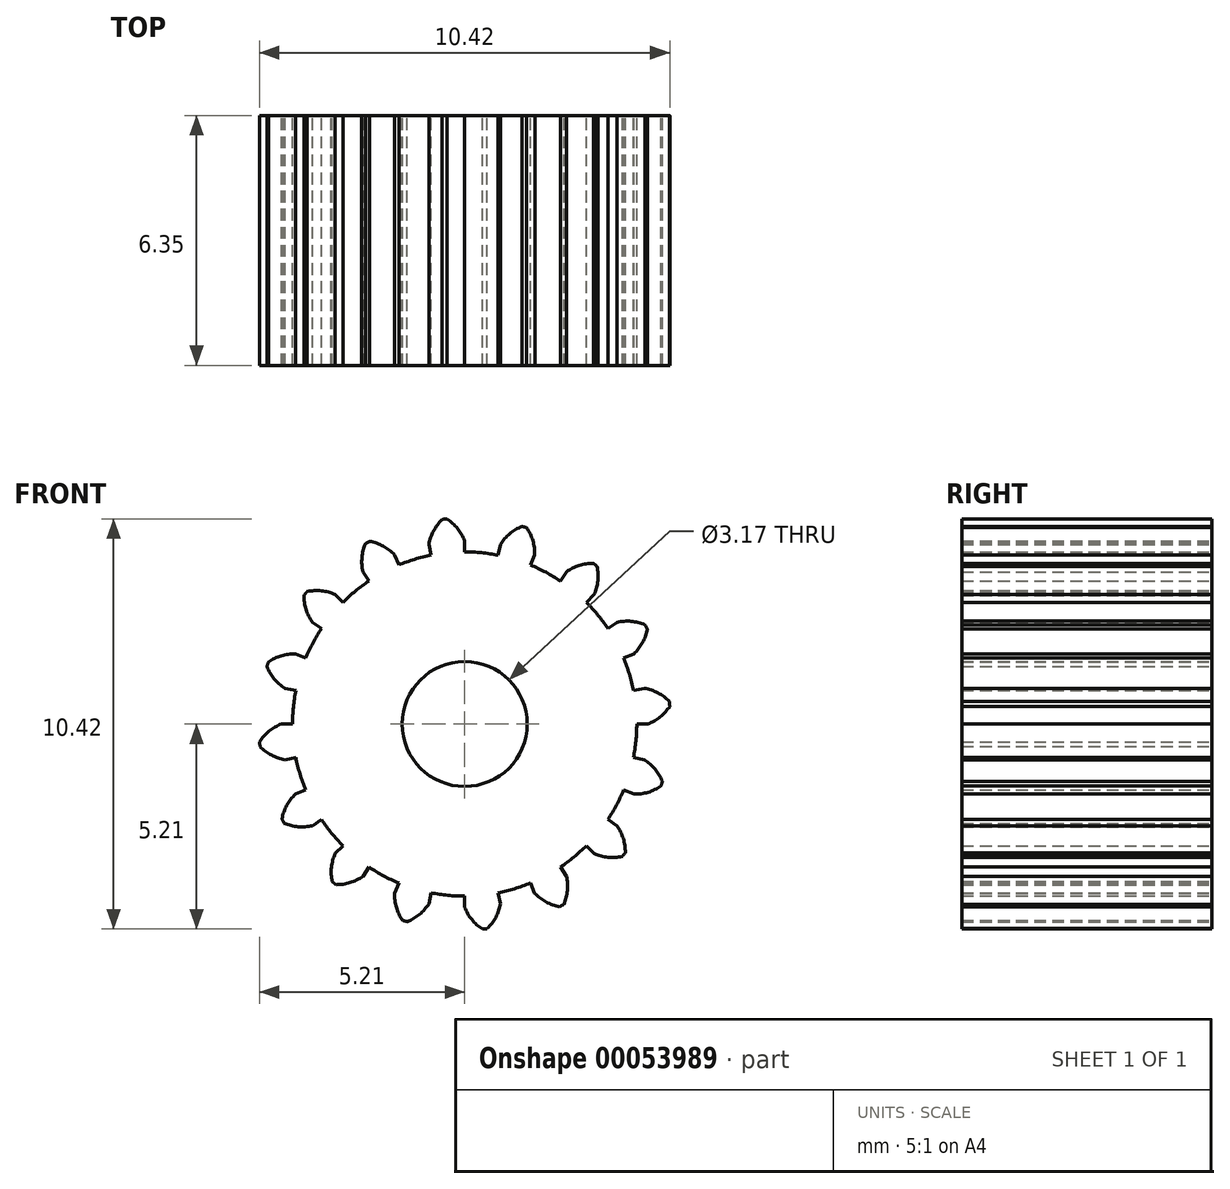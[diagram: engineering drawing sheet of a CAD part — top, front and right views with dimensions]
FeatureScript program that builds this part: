
annotation { "Feature Type Name" : "Feature", "Feature Type Description" : "" }
export const myFeature = defineFeature(function(context is Context, id is Id, definition is map)
    precondition{}
    {
        {
            var Q0;
            Q0=qCreatedBy(makeId("Front.planeOp"),FACE);
            var sketch = newSketch(context, id + "F0", { "sketchPlane" : qUnion([Q0])});
            skArc(sketch, "E0", {"start": v(-0.45, 5.21) * mm, "mid": v(-0.48, 5.2) * mm, "end": v(-0.51, 5.2) * mm});
            skArc(sketch, "E1", {"start": v(-0.85, 4.29) * mm, "mid": v(-1.27, 4.18) * mm, "end": v(-1.67, 4.04) * mm});
            skArc(sketch, "E2.trimOffspring", {"start": v(0, 4.65) * mm, "mid": v(-0.18, 4.97) * mm, "end": v(-0.45, 5.21) * mm});
            skLineSegment(sketch, "E3", {"start": v(0, 4.65) * mm, "end": v(0, 4.37) * mm});
            skLineSegment(sketch, "E4.MirrorCS", {"start": v(-0.9, 4.56) * mm, "end": v(-0.85, 4.29) * mm});
            skArc(sketch, "E5.MirrorCS", {"start": v(-0.9, 4.56) * mm, "mid": v(-0.8, 4.9) * mm, "end": v(-0.57, 5.2) * mm});
            skArc(sketch, "E6.MirrorCS", {"start": v(-0.57, 5.2) * mm, "mid": v(-0.54, 5.2) * mm, "end": v(-0.51, 5.2) * mm});
            skLineSegment(sketch, "E7.1.0", {"start": v(-2.59, 3.87) * mm, "end": v(-2.43, 3.64) * mm});
            skArc(sketch, "E7.1.1", {"start": v(-2.59, 3.87) * mm, "mid": v(-2.6, 4.23) * mm, "end": v(-2.52, 4.58) * mm});
            skArc(sketch, "E7.1.2", {"start": v(-2.41, 4.64) * mm, "mid": v(-2.44, 4.63) * mm, "end": v(-2.47, 4.61) * mm});
            skArc(sketch, "E7.1.3", {"start": v(-2.52, 4.58) * mm, "mid": v(-2.5, 4.6) * mm, "end": v(-2.47, 4.61) * mm});
            skArc(sketch, "E7.1.4", {"start": v(-1.78, 4.3) * mm, "mid": v(-2.07, 4.52) * mm, "end": v(-2.41, 4.64) * mm});
            skLineSegment(sketch, "E7.1.5", {"start": v(-1.78, 4.3) * mm, "end": v(-1.67, 4.04) * mm});
            skLineSegment(sketch, "E7.2.0", {"start": v(-3.87, 2.59) * mm, "end": v(-3.64, 2.43) * mm});
            skArc(sketch, "E7.2.1", {"start": v(-3.87, 2.59) * mm, "mid": v(-4.03, 2.91) * mm, "end": v(-4.08, 3.27) * mm});
            skArc(sketch, "E7.2.2", {"start": v(-4, 3.37) * mm, "mid": v(-4.02, 3.34) * mm, "end": v(-4.04, 3.32) * mm});
            skArc(sketch, "E7.2.3", {"start": v(-4.08, 3.27) * mm, "mid": v(-4.06, 3.3) * mm, "end": v(-4.04, 3.32) * mm});
            skArc(sketch, "E7.2.4", {"start": v(-3.3, 3.3) * mm, "mid": v(-3.64, 3.38) * mm, "end": v(-4, 3.37) * mm});
            skLineSegment(sketch, "E7.2.5", {"start": v(-3.3, 3.3) * mm, "end": v(-3.1, 3.1) * mm});
            skLineSegment(sketch, "E7.3.0", {"start": v(-4.56, 0.9) * mm, "end": v(-4.29, 0.85) * mm});
            skArc(sketch, "E7.3.1", {"start": v(-4.56, 0.9) * mm, "mid": v(-4.84, 1.15) * mm, "end": v(-5.02, 1.46) * mm});
            skArc(sketch, "E7.3.2", {"start": v(-4.99, 1.58) * mm, "mid": v(-5, 1.55) * mm, "end": v(-5, 1.52) * mm});
            skArc(sketch, "E7.3.3", {"start": v(-5.02, 1.46) * mm, "mid": v(-5.01, 1.49) * mm, "end": v(-5, 1.52) * mm});
            skArc(sketch, "E7.3.4", {"start": v(-4.3, 1.78) * mm, "mid": v(-4.66, 1.73) * mm, "end": v(-4.99, 1.58) * mm});
            skLineSegment(sketch, "E7.3.5", {"start": v(-4.3, 1.78) * mm, "end": v(-4.04, 1.67) * mm});
            skLineSegment(sketch, "E7.4.0", {"start": v(-4.56, -0.9) * mm, "end": v(-4.29, -0.85) * mm});
            skArc(sketch, "E7.4.1", {"start": v(-4.56, -0.9) * mm, "mid": v(-4.9, -0.8) * mm, "end": v(-5.2, -0.57) * mm});
            skArc(sketch, "E7.4.2", {"start": v(-5.21, -0.45) * mm, "mid": v(-5.2, -0.48) * mm, "end": v(-5.2, -0.51) * mm});
            skArc(sketch, "E7.4.3", {"start": v(-5.2, -0.57) * mm, "mid": v(-5.2, -0.54) * mm, "end": v(-5.2, -0.51) * mm});
            skArc(sketch, "E7.4.4", {"start": v(-4.65, 0) * mm, "mid": v(-4.97, -0.18) * mm, "end": v(-5.21, -0.45) * mm});
            skLineSegment(sketch, "E7.4.5", {"start": v(-4.65, 0) * mm, "end": v(-4.37, 0) * mm});
            skLineSegment(sketch, "E7.5.0", {"start": v(-3.87, -2.59) * mm, "end": v(-3.64, -2.43) * mm});
            skArc(sketch, "E7.5.1", {"start": v(-3.87, -2.59) * mm, "mid": v(-4.23, -2.6) * mm, "end": v(-4.58, -2.52) * mm});
            skArc(sketch, "E7.5.2", {"start": v(-4.64, -2.41) * mm, "mid": v(-4.63, -2.44) * mm, "end": v(-4.61, -2.47) * mm});
            skArc(sketch, "E7.5.3", {"start": v(-4.58, -2.52) * mm, "mid": v(-4.6, -2.5) * mm, "end": v(-4.61, -2.47) * mm});
            skArc(sketch, "E7.5.4", {"start": v(-4.3, -1.78) * mm, "mid": v(-4.52, -2.07) * mm, "end": v(-4.64, -2.41) * mm});
            skLineSegment(sketch, "E7.5.5", {"start": v(-4.3, -1.78) * mm, "end": v(-4.04, -1.67) * mm});
            skLineSegment(sketch, "E7.6.0", {"start": v(-2.59, -3.87) * mm, "end": v(-2.43, -3.64) * mm});
            skArc(sketch, "E7.6.1", {"start": v(-2.59, -3.87) * mm, "mid": v(-2.91, -4.03) * mm, "end": v(-3.27, -4.08) * mm});
            skArc(sketch, "E7.6.2", {"start": v(-3.37, -4) * mm, "mid": v(-3.34, -4.02) * mm, "end": v(-3.32, -4.04) * mm});
            skArc(sketch, "E7.6.3", {"start": v(-3.27, -4.08) * mm, "mid": v(-3.3, -4.06) * mm, "end": v(-3.32, -4.04) * mm});
            skArc(sketch, "E7.6.4", {"start": v(-3.3, -3.3) * mm, "mid": v(-3.38, -3.64) * mm, "end": v(-3.37, -4) * mm});
            skLineSegment(sketch, "E7.6.5", {"start": v(-3.3, -3.3) * mm, "end": v(-3.1, -3.1) * mm});
            skLineSegment(sketch, "E7.7.0", {"start": v(-0.9, -4.56) * mm, "end": v(-0.85, -4.29) * mm});
            skArc(sketch, "E7.7.1", {"start": v(-0.9, -4.56) * mm, "mid": v(-1.15, -4.84) * mm, "end": v(-1.46, -5.02) * mm});
            skArc(sketch, "E7.7.2", {"start": v(-1.58, -4.99) * mm, "mid": v(-1.55, -5) * mm, "end": v(-1.52, -5) * mm});
            skArc(sketch, "E7.7.3", {"start": v(-1.46, -5.02) * mm, "mid": v(-1.49, -5.01) * mm, "end": v(-1.52, -5) * mm});
            skArc(sketch, "E7.7.4", {"start": v(-1.78, -4.3) * mm, "mid": v(-1.73, -4.66) * mm, "end": v(-1.58, -4.99) * mm});
            skLineSegment(sketch, "E7.7.5", {"start": v(-1.78, -4.3) * mm, "end": v(-1.67, -4.04) * mm});
            skLineSegment(sketch, "E7.8.0", {"start": v(0.9, -4.56) * mm, "end": v(0.85, -4.29) * mm});
            skArc(sketch, "E7.8.1", {"start": v(0.9, -4.56) * mm, "mid": v(0.8, -4.9) * mm, "end": v(0.57, -5.2) * mm});
            skArc(sketch, "E7.8.2", {"start": v(0.45, -5.21) * mm, "mid": v(0.48, -5.2) * mm, "end": v(0.51, -5.2) * mm});
            skArc(sketch, "E7.8.3", {"start": v(0.57, -5.2) * mm, "mid": v(0.54, -5.2) * mm, "end": v(0.51, -5.2) * mm});
            skArc(sketch, "E7.8.4", {"start": v(0, -4.65) * mm, "mid": v(0.18, -4.97) * mm, "end": v(0.45, -5.21) * mm});
            skLineSegment(sketch, "E7.8.5", {"start": v(0, -4.65) * mm, "end": v(0, -4.37) * mm});
            skLineSegment(sketch, "E7.9.0", {"start": v(2.59, -3.87) * mm, "end": v(2.43, -3.64) * mm});
            skArc(sketch, "E7.9.1", {"start": v(2.59, -3.87) * mm, "mid": v(2.6, -4.23) * mm, "end": v(2.52, -4.58) * mm});
            skArc(sketch, "E7.9.2", {"start": v(2.41, -4.64) * mm, "mid": v(2.44, -4.63) * mm, "end": v(2.47, -4.61) * mm});
            skArc(sketch, "E7.9.3", {"start": v(2.52, -4.58) * mm, "mid": v(2.5, -4.6) * mm, "end": v(2.47, -4.61) * mm});
            skArc(sketch, "E7.9.4", {"start": v(1.78, -4.3) * mm, "mid": v(2.07, -4.52) * mm, "end": v(2.41, -4.64) * mm});
            skLineSegment(sketch, "E7.9.5", {"start": v(1.78, -4.3) * mm, "end": v(1.67, -4.04) * mm});
            skLineSegment(sketch, "E7.10.0", {"start": v(3.87, -2.59) * mm, "end": v(3.64, -2.43) * mm});
            skArc(sketch, "E7.10.1", {"start": v(3.87, -2.59) * mm, "mid": v(4.03, -2.91) * mm, "end": v(4.08, -3.27) * mm});
            skArc(sketch, "E7.10.2", {"start": v(4, -3.37) * mm, "mid": v(4.02, -3.34) * mm, "end": v(4.04, -3.32) * mm});
            skArc(sketch, "E7.10.3", {"start": v(4.08, -3.27) * mm, "mid": v(4.06, -3.3) * mm, "end": v(4.04, -3.32) * mm});
            skArc(sketch, "E7.10.4", {"start": v(3.3, -3.3) * mm, "mid": v(3.64, -3.38) * mm, "end": v(4, -3.37) * mm});
            skLineSegment(sketch, "E7.10.5", {"start": v(3.3, -3.3) * mm, "end": v(3.1, -3.1) * mm});
            skLineSegment(sketch, "E7.11.0", {"start": v(4.56, -0.9) * mm, "end": v(4.29, -0.85) * mm});
            skArc(sketch, "E7.11.1", {"start": v(4.56, -0.9) * mm, "mid": v(4.84, -1.15) * mm, "end": v(5.02, -1.46) * mm});
            skArc(sketch, "E7.11.2", {"start": v(4.99, -1.58) * mm, "mid": v(5, -1.55) * mm, "end": v(5, -1.52) * mm});
            skArc(sketch, "E7.11.3", {"start": v(5.02, -1.46) * mm, "mid": v(5.01, -1.49) * mm, "end": v(5, -1.52) * mm});
            skArc(sketch, "E7.11.4", {"start": v(4.3, -1.78) * mm, "mid": v(4.66, -1.73) * mm, "end": v(4.99, -1.58) * mm});
            skLineSegment(sketch, "E7.11.5", {"start": v(4.3, -1.78) * mm, "end": v(4.04, -1.67) * mm});
            skLineSegment(sketch, "E7.12.0", {"start": v(4.56, 0.9) * mm, "end": v(4.29, 0.85) * mm});
            skArc(sketch, "E7.12.1", {"start": v(4.56, 0.9) * mm, "mid": v(4.9, 0.8) * mm, "end": v(5.2, 0.57) * mm});
            skArc(sketch, "E7.12.2", {"start": v(5.21, 0.45) * mm, "mid": v(5.2, 0.48) * mm, "end": v(5.2, 0.51) * mm});
            skArc(sketch, "E7.12.3", {"start": v(5.2, 0.57) * mm, "mid": v(5.2, 0.54) * mm, "end": v(5.2, 0.51) * mm});
            skArc(sketch, "E7.12.4", {"start": v(4.65, 0) * mm, "mid": v(4.97, 0.18) * mm, "end": v(5.21, 0.45) * mm});
            skLineSegment(sketch, "E7.12.5", {"start": v(4.65, 0) * mm, "end": v(4.37, 0) * mm});
            skLineSegment(sketch, "E7.13.0", {"start": v(3.87, 2.59) * mm, "end": v(3.64, 2.43) * mm});
            skArc(sketch, "E7.13.1", {"start": v(3.87, 2.59) * mm, "mid": v(4.23, 2.6) * mm, "end": v(4.58, 2.52) * mm});
            skArc(sketch, "E7.13.2", {"start": v(4.64, 2.41) * mm, "mid": v(4.63, 2.44) * mm, "end": v(4.61, 2.47) * mm});
            skArc(sketch, "E7.13.3", {"start": v(4.58, 2.52) * mm, "mid": v(4.6, 2.5) * mm, "end": v(4.61, 2.47) * mm});
            skArc(sketch, "E7.13.4", {"start": v(4.3, 1.78) * mm, "mid": v(4.52, 2.07) * mm, "end": v(4.64, 2.41) * mm});
            skLineSegment(sketch, "E7.13.5", {"start": v(4.3, 1.78) * mm, "end": v(4.04, 1.67) * mm});
            skLineSegment(sketch, "E7.14.0", {"start": v(2.59, 3.87) * mm, "end": v(2.43, 3.64) * mm});
            skArc(sketch, "E7.14.1", {"start": v(2.59, 3.87) * mm, "mid": v(2.91, 4.03) * mm, "end": v(3.27, 4.08) * mm});
            skArc(sketch, "E7.14.2", {"start": v(3.37, 4) * mm, "mid": v(3.34, 4.02) * mm, "end": v(3.32, 4.04) * mm});
            skArc(sketch, "E7.14.3", {"start": v(3.27, 4.08) * mm, "mid": v(3.3, 4.06) * mm, "end": v(3.32, 4.04) * mm});
            skArc(sketch, "E7.14.4", {"start": v(3.3, 3.3) * mm, "mid": v(3.38, 3.64) * mm, "end": v(3.37, 4) * mm});
            skLineSegment(sketch, "E7.14.5", {"start": v(3.3, 3.3) * mm, "end": v(3.1, 3.1) * mm});
            skLineSegment(sketch, "E7.15.0", {"start": v(0.9, 4.56) * mm, "end": v(0.85, 4.29) * mm});
            skArc(sketch, "E7.15.1", {"start": v(0.9, 4.56) * mm, "mid": v(1.15, 4.84) * mm, "end": v(1.46, 5.02) * mm});
            skArc(sketch, "E7.15.2", {"start": v(1.58, 4.99) * mm, "mid": v(1.55, 5) * mm, "end": v(1.52, 5) * mm});
            skArc(sketch, "E7.15.3", {"start": v(1.46, 5.02) * mm, "mid": v(1.49, 5.01) * mm, "end": v(1.52, 5) * mm});
            skArc(sketch, "E7.15.4", {"start": v(1.78, 4.3) * mm, "mid": v(1.73, 4.66) * mm, "end": v(1.58, 4.99) * mm});
            skLineSegment(sketch, "E7.15.5", {"start": v(1.78, 4.3) * mm, "end": v(1.67, 4.04) * mm});
            skArc(sketch, "E8.trimOffspring", {"start": v(0.85, 4.29) * mm, "mid": v(0.43, 4.35) * mm, "end": v(0, 4.37) * mm});
            skArc(sketch, "E9.trimOffspring", {"start": v(-2.43, 3.64) * mm, "mid": v(-2.77, 3.38) * mm, "end": v(-3.1, 3.1) * mm});
            skArc(sketch, "E10.trimOffspring", {"start": v(-3.64, 2.43) * mm, "mid": v(-3.86, 2.06) * mm, "end": v(-4.04, 1.67) * mm});
            skArc(sketch, "E11.trimOffspring", {"start": v(-4.29, 0.85) * mm, "mid": v(-4.35, 0.43) * mm, "end": v(-4.37, 0) * mm});
            skArc(sketch, "E12.trimOffspring", {"start": v(-4.29, -0.85) * mm, "mid": v(-4.18, -1.27) * mm, "end": v(-4.04, -1.67) * mm});
            skArc(sketch, "E13.trimOffspring", {"start": v(-3.64, -2.43) * mm, "mid": v(-3.38, -2.77) * mm, "end": v(-3.1, -3.1) * mm});
            skArc(sketch, "E14.trimOffspring", {"start": v(-2.43, -3.64) * mm, "mid": v(-2.06, -3.86) * mm, "end": v(-1.67, -4.04) * mm});
            skArc(sketch, "E15.trimOffspring", {"start": v(-0.85, -4.29) * mm, "mid": v(-0.43, -4.35) * mm, "end": v(0, -4.37) * mm});
            skArc(sketch, "E16.trimOffspring", {"start": v(0.85, -4.29) * mm, "mid": v(1.27, -4.18) * mm, "end": v(1.67, -4.04) * mm});
            skArc(sketch, "E17.trimOffspring", {"start": v(2.43, -3.64) * mm, "mid": v(2.77, -3.38) * mm, "end": v(3.1, -3.1) * mm});
            skArc(sketch, "E18.trimOffspring", {"start": v(3.64, -2.43) * mm, "mid": v(3.86, -2.06) * mm, "end": v(4.04, -1.67) * mm});
            skArc(sketch, "E19.trimOffspring", {"start": v(4.29, -0.85) * mm, "mid": v(4.35, -0.43) * mm, "end": v(4.37, 0) * mm});
            skArc(sketch, "E20.trimOffspring", {"start": v(4.29, 0.85) * mm, "mid": v(4.18, 1.27) * mm, "end": v(4.04, 1.67) * mm});
            skArc(sketch, "E21.trimOffspring", {"start": v(3.64, 2.43) * mm, "mid": v(3.38, 2.77) * mm, "end": v(3.1, 3.1) * mm});
            skArc(sketch, "E22.trimOffspring", {"start": v(2.43, 3.64) * mm, "mid": v(2.06, 3.86) * mm, "end": v(1.67, 4.04) * mm});
            skCircle(sketch, "E23", {"center": v(0, 0) * mm, "radius": 1.59 * mm});
            skSolve(sketch);
        }
        {
            var Q0;
            Q0=makeQuery(id+"F0.imprint","IMPRINT",FACE,{"disambiguationData":[TD([[makeQuery(id+"F0.imprint","IMPRINT",EDGE,{"derivedFrom":sQuery(id+"F0.wireOp",EDGE,"E0")}),1.0]])]});
            extrude(context, id + "F1", {"entities" : qUnion([Q0]), "depth" : 6.35 * mm});
        }
    });
